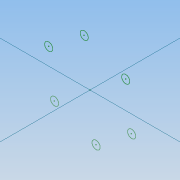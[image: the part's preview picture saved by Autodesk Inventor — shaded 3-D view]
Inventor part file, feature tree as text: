
AUTODESK INVENTOR PART (.ipt)
format: ipt  version: 2014 SP2 (Build 180246200, 246)  size: 57,344 bytes
history: native  units: in
note: dims shown in document units (in); Inventor stores cm internally (conversion verified against a paired STEP export)
features: reference x6, sketch x1
ambient origin geometry x8: Origin, YZ Plane, XZ Plane, XY Plane, X Axis, Y Axis, Z Axis, Center Point
feature tree (7):
  sketch  "Sketch1"
  reference  "Reference1"
  reference  "Reference2"
  reference  "Reference3"
  reference  "Reference4"
  reference  "Reference5"
  reference  "Reference6"
